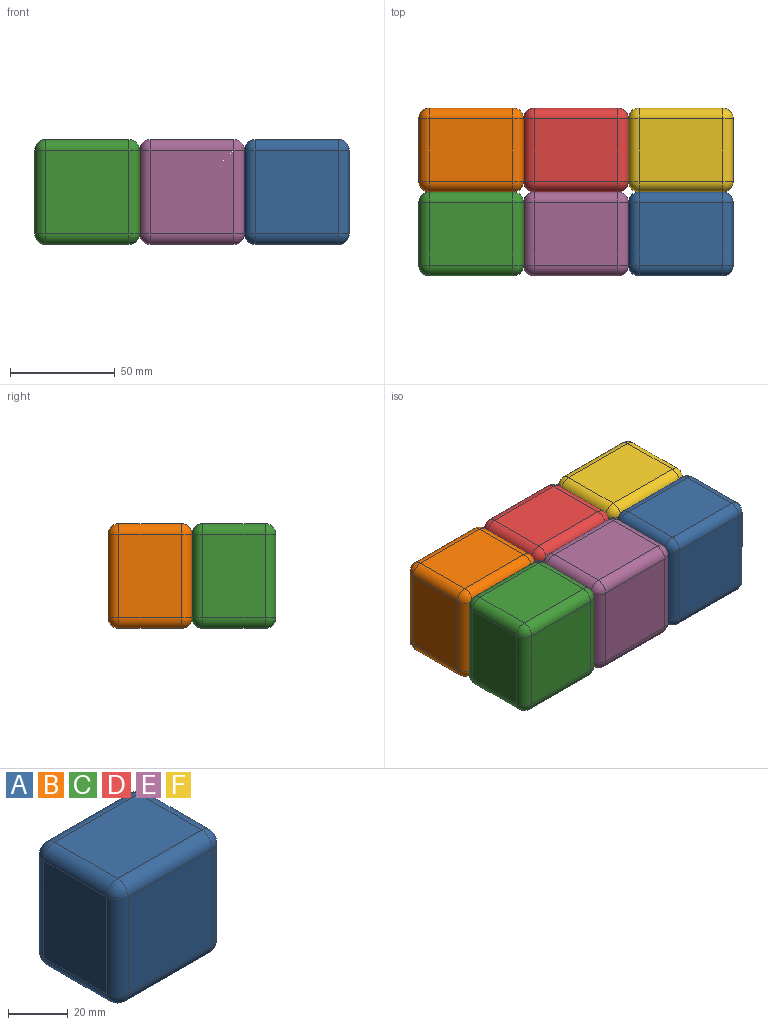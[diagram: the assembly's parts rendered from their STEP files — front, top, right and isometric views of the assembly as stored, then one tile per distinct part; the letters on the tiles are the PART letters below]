
ASSEMBLY  parts=6 mates=3
PART A: 26 faces, bbox 50x40x50 mm
  f0: plane 39.84x29.84mm, normal (-1,0,0), area 1188.8mm2, adj f14,f19,f22,f25
  f1: plane 39.84x39.84mm, normal (0,-1,0), area 1587.2mm2, adj f11,f20,f21,f25
  f2: plane 39.84x29.84mm, normal (1,0,0), area 1188.8mm2, adj f6,f10,f11,f12
  f3: plane 39.84x39.84mm, normal (0,1,0), area 1587.2mm2, adj f6,f9,f13,f14
  f4: plane 39.84x29.84mm, normal (0,0,1), area 1188.8mm2, adj f9,f10,f19,f20
  f5: plane 39.84x29.84mm, normal (0,0,-1), area 1188.8mm2, adj f12,f13,f21,f22
  f6: cylinder r=5.08mm len=39.84mm, axis (0,0,-1), area 317.9mm2, adj f2,f3,f7,f8
  f7: sphere r=5.08mm, area 40.5mm2, adj f6,f9,f10
  f8: sphere r=5.08mm, area 40.5mm2, adj f6,f12,f13
  f9: cylinder r=5.08mm len=39.84mm, axis (1,0,0), area 317.9mm2, adj f3,f4,f7,f15
  f10: cylinder r=5.08mm len=29.84mm, axis (0,-1,0), area 238.1mm2, adj f2,f4,f7,f16
  f11: cylinder r=5.08mm len=39.84mm, axis (0,0,1), area 317.9mm2, adj f1,f2,f16,f17
  f12: cylinder r=5.08mm len=29.84mm, axis (0,1,0), area 238.1mm2, adj f2,f5,f8,f17
  f13: cylinder r=5.08mm len=39.84mm, axis (-1,0,0), area 317.9mm2, adj f3,f5,f8,f18
  f14: cylinder r=5.08mm len=39.84mm, axis (0,0,1), area 317.9mm2, adj f0,f3,f15,f18
  f15: sphere r=5.08mm, area 40.5mm2, adj f9,f14,f19
  f16: sphere r=5.08mm, area 40.5mm2, adj f10,f11,f20
  f17: sphere r=5.08mm, area 40.5mm2, adj f11,f12,f21
  f18: sphere r=5.08mm, area 40.5mm2, adj f13,f14,f22
  f19: cylinder r=5.08mm len=29.84mm, axis (0,1,0), area 238.1mm2, adj f0,f4,f15,f23
  f20: cylinder r=5.08mm len=39.84mm, axis (-1,0,0), area 317.9mm2, adj f1,f4,f16,f23
  f21: cylinder r=5.08mm len=39.84mm, axis (1,0,0), area 317.9mm2, adj f1,f5,f17,f24
  f22: cylinder r=5.08mm len=29.84mm, axis (0,-1,0), area 238.1mm2, adj f0,f5,f18,f24
  f23: sphere r=5.08mm, area 40.5mm2, adj f19,f20,f25
  f24: sphere r=5.08mm, area 40.5mm2, adj f21,f22,f25
  f25: cylinder r=5.08mm len=39.84mm, axis (0,0,-1), area 317.9mm2, adj f0,f1,f23,f24
PART B: same geometry as A
PART C: same geometry as A
PART D: same geometry as A
PART E: same geometry as A
PART F: same geometry as A
PLACE A t=(114.62,-91.61,-100.08)mm
PLACE B t=(14.62,-51.61,-100.08)mm
PLACE C t=(14.62,-91.61,-100.08)mm
PLACE D t=(64.62,-51.61,-100.08)mm
PLACE E t=(64.62,-91.61,-100.08)mm
PLACE F t=(114.62,-51.61,-100.08)mm
MATE fastened D.f2 <-> F.f0  axis (1,0,0) through (89.62,-51.61,-75.08)mm
MATE fastened C.f3 <-> B.f1  axis (0,1,0) through (14.62,-71.61,-75.08)mm
MATE fastened F.f1 <-> A.f3  axis (0,-1,0) through (114.62,-71.61,-75.08)mm
